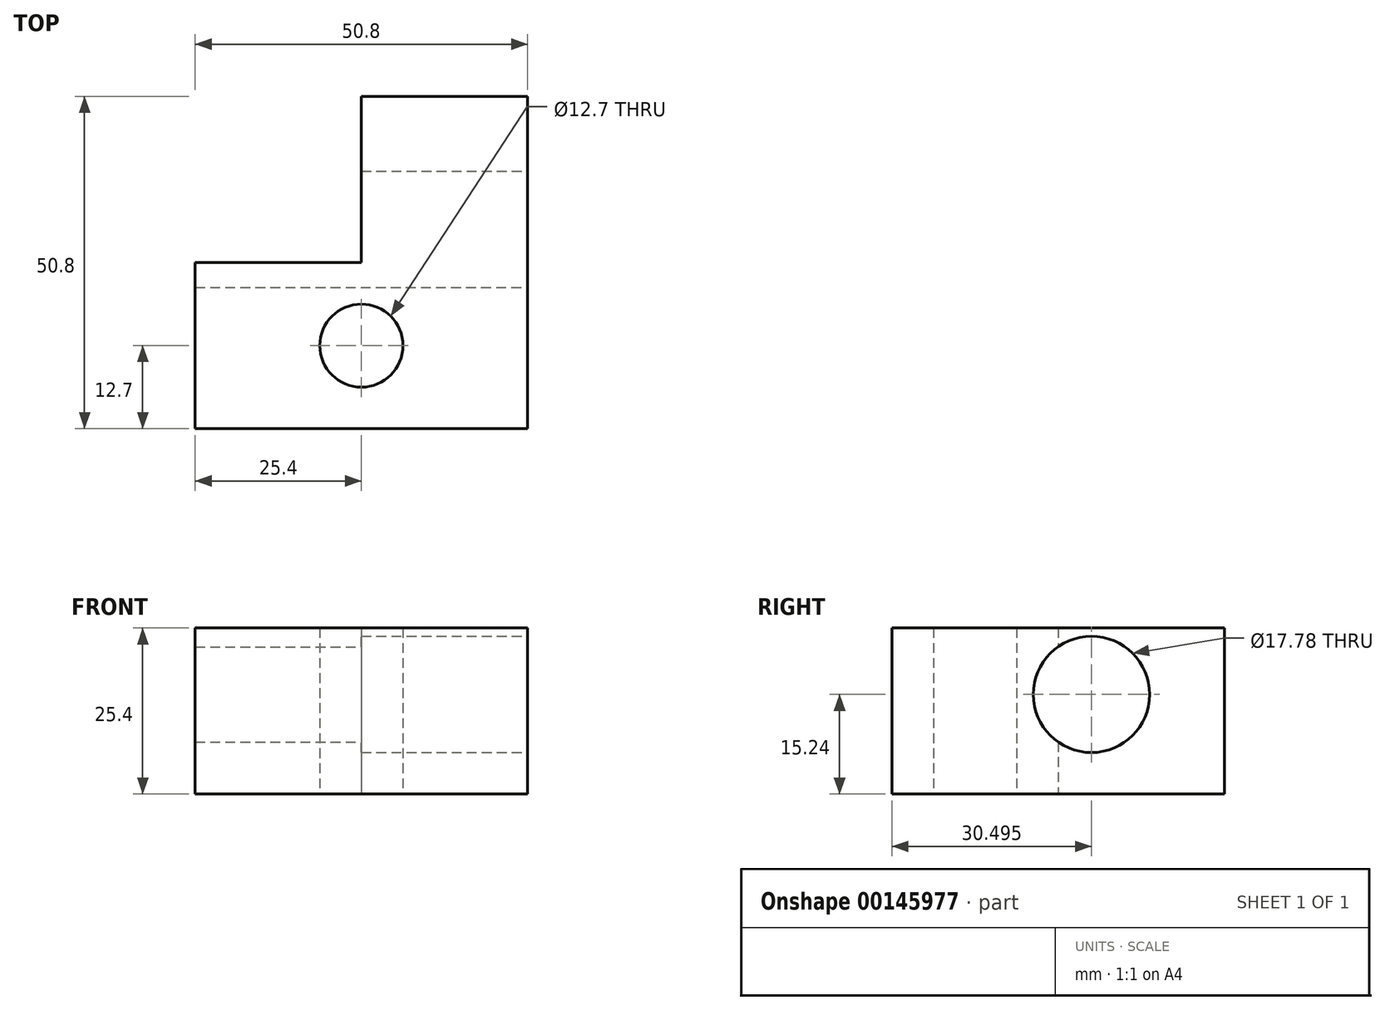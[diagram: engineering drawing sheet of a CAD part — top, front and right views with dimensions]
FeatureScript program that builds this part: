
annotation { "Feature Type Name" : "Feature", "Feature Type Description" : "" }
export const myFeature = defineFeature(function(context is Context, id is Id, definition is map)
    precondition{}
    {
        {
            var Q0;
            Q0=qCreatedBy(makeId("Top.planeOp"),FACE);
            var sketch = newSketch(context, id + "F0", { "sketchPlane" : qUnion([Q0])});
            skLineSegment(sketch, "E0", {"start": v(0, 0) * mm, "end": v(-50.8, 0) * mm});
            skLineSegment(sketch, "E1", {"start": v(-50.8, 0) * mm, "end": v(-50.8, 25.4) * mm});
            skLineSegment(sketch, "E2", {"start": v(-50.8, 25.4) * mm, "end": v(-25.4, 25.4) * mm});
            skLineSegment(sketch, "E3", {"start": v(-25.4, 25.4) * mm, "end": v(-25.4, 50.8) * mm});
            skLineSegment(sketch, "E4", {"start": v(-25.4, 50.8) * mm, "end": v(0, 50.8) * mm});
            skLineSegment(sketch, "E5", {"start": v(0, 50.8) * mm, "end": v(0, 0) * mm});
            skCircle(sketch, "E6", {"center": v(-25.4, 12.7) * mm, "radius": 6.35 * mm});
            skSolve(sketch);
        }
        {
            var Q0;
            Q0 = qSketchRegion(id + "F0", true);
            extrude(context, id + "F1", {"entities" : qUnion([Q0]), "depth" : 25.4 * mm});
        }
        {
            var Q0;
            Q0=makeQuery(id+"F1.opExtrude","SWEPT_FACE",FACE,{"disambiguationData":[OSD([sQuery(id+"F0.wireOp",EDGE,"E5")])]});
            var sketch = newSketch(context, id + "F2", { "sketchPlane" : qUnion([Q0])});
            skCircle(sketch, "E7", {"center": v(30.5, 15.24) * mm, "radius": 8.9 * mm});
            skSolve(sketch);
        }
        {
            var Q0;
            Q0 = qSketchRegion(id + "F2", true);
            extrude(context, id + "F3", {"entities" : qUnion([Q0]), "operationType" : NewBodyOperationType.REMOVE, "oppositeDirection" : true, "depth" : 50.8 * mm});
        }
    });
